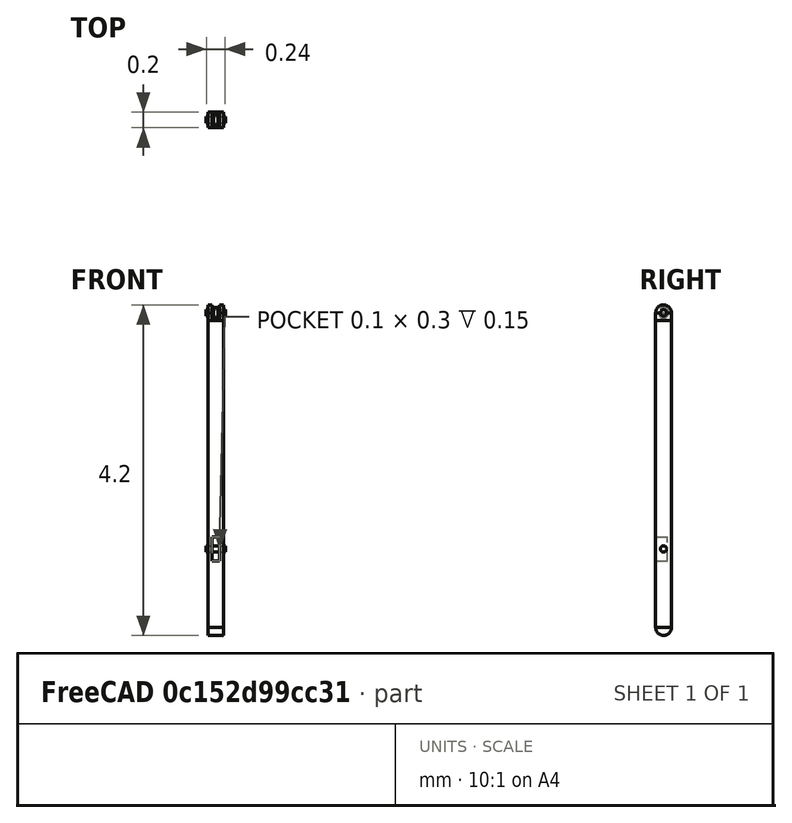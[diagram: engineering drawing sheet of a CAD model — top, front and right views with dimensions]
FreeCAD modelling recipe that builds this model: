
FCSTD DOCUMENT  (FreeCAD 0.14R3702 (Git))
Label: arm2
License: CC-BY 3.0
LicenseURL: http://creativecommons.org/licenses/by/3.0/
objects: Part::Cylinder×6, Part::Box×4, Part::Cut×1
note: 11 computed .brp shape members not serialized (recipe doc carries the construction recipe); baked Part::Feature solids carry a one-line shape summary decoded from their .brp

FEATURE [Part::Cylinder] Cylinder001
  Angle = 180
  Height = 0.2
  Placement = pos=(-0.1,0,0) rot=(-0.57735,0.57735,-0.57735;2.0944rad)
  Radius = 0.1
FEATURE [Part::Cylinder] Cylinder
  Angle = 360
  Height = 0.25
  Placement = pos=(-0.125,0,1) rot=(0.57735,0.57735,0.57735;2.0944rad)
  Radius = 0.04
FEATURE [Part::Cylinder] Cylinder002
  Angle = 180
  Height = 0.05
  Placement = pos=(0.05,0,4) rot=(0.57735,0.57735,0.57735;2.0944rad)
  Radius = 0.1
FEATURE [Part::Box] Box004  label="Cube004"
  Height = 0.3
  Length = 0.1
  Placement = pos=(-0.05,-0.1,0.85) rot=(0,0,1;0rad)
  Width = 0.15
FEATURE [Part::Box] Box005  label="Cube005"
  Height = 3.9
  Length = 0.2
  Placement = pos=(-0.1,-0.1,0) rot=(0,0,1;0rad)
  Width = 0.2
FEATURE [Part::Cut] Cut
  Base = -> Box005
  Tool = -> Box004
FEATURE [Part::Box] Box  label="Cube"
  Height = 0.1
  Length = 0.05
  Placement = pos=(0.05,-0.1,3.9) rot=(0,0,1;0rad)
  Width = 0.2
FEATURE [Part::Box] Box006  label="Cube006"
  Height = 0.1
  Length = 0.05
  Placement = pos=(-0.1,-0.1,3.9) rot=(0,0,1;0rad)
  Width = 0.2
FEATURE [Part::Cylinder] Cylinder004
  Angle = 180
  Height = 0.05
  Placement = pos=(-0.1,0,4) rot=(0.57735,0.57735,0.57735;2.0944rad)
  Radius = 0.1
FEATURE [Part::Cylinder] Cylinder005
  Angle = 360
  Height = 0.25
  Placement = pos=(-0.125,0,4) rot=(0.57735,0.57735,0.57735;2.0944rad)
  Radius = 0.04
FEATURE [Part::Cylinder] Cylinder006
  Angle = 360
  Height = 0.06
  Placement = pos=(-0.03,0,4) rot=(0.57735,0.57735,0.57735;2.0944rad)
  Radius = 0.065
